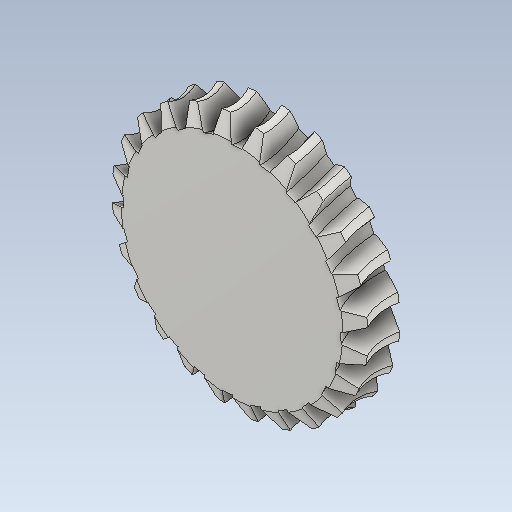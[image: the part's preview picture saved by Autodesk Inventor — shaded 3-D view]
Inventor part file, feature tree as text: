
AUTODESK INVENTOR PART (.ipt)
format: ipt  version: 2021 (Build 250183000, 183)  size: 484,352 bytes
history: native  units: mm (DEFAULTED — no unit token found)
features: other x8, plane x3, pattern_circular x1, sketch x1
ambient origin geometry x5: Origin, X Axis, Y Axis, Z Axis, Center Point
bodies: Solid1 (feature_tree)
feature tree (13):
  other  "Tooth Plane"
  other  "Base Body Sketch"
  other  "Base Body"
  other  "Base Body2"
  plane  "Work Plane13"
  other  "Tooth"
  pattern_circular  "Tooth Pattern"  [2 undecoded]
  plane  "Work Plane14"
  plane  "Work Plane15"
  other  "Tooth Sketch"
  sketch  "Sketch8"  dims[d35=90.0deg d37=-1.973956mm d38=68.0168mm d39=3.490659mm d40=15.2mm d41=20.0mm d42=3.769911mm d43=90.0deg d44=240.0mm d46=360.0deg d50=4.297754mm d68=68.0168mm d69=0.0mm d73=0.0mm d75=1.308997mm d77=96.0mm d78=20.0mm d79=0.0mm d80=0.0mm d81=0.0mm d82=0.0mm d83=1.308997mm d84=0.0mm d85=180.0deg d86=68.0168mm d87=108.0336mm d89=32.0mm d90=90.0deg d92=20.0mm d93=68.0168mm]
  other  "Srf1"
  other  "Pitch Diameter"
note: 2 required parameter values undecoded (feature->parameter linkage not recoverable at this tier; creation-order binding heuristic only, values carry confidence <= 0.55)
